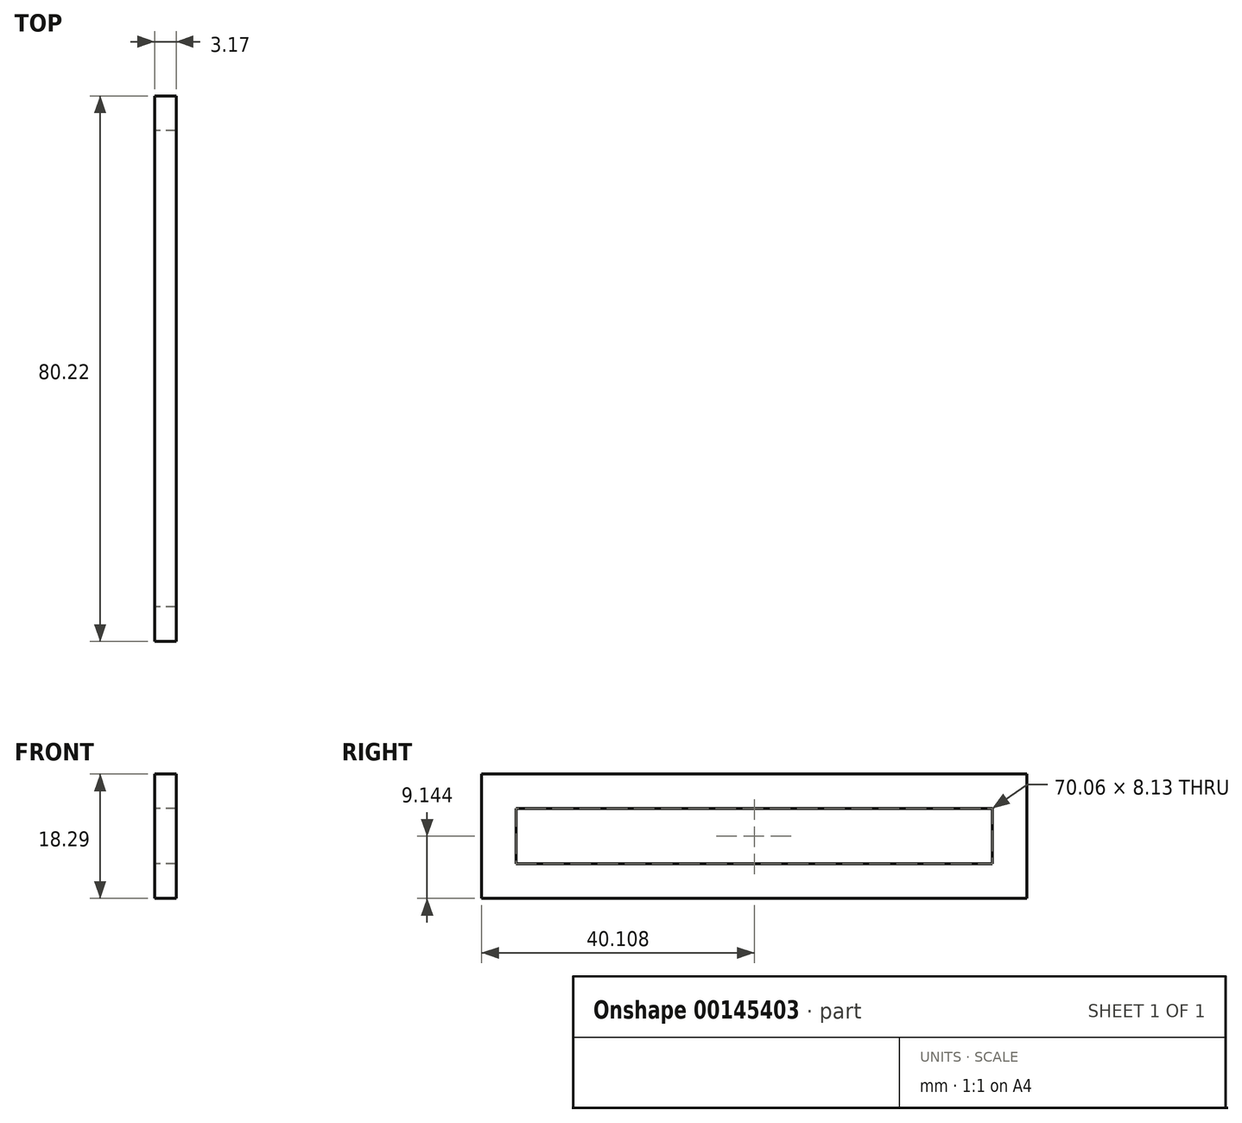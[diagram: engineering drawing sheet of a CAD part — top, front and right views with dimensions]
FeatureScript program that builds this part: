
annotation { "Feature Type Name" : "Feature", "Feature Type Description" : "" }
export const myFeature = defineFeature(function(context is Context, id is Id, definition is map)
    precondition{}
    {
        {
            var Q0;
            Q0=qCreatedBy(makeId("Right.planeOp"),FACE);
            var sketch = newSketch(context, id + "F0", { "sketchPlane" : qUnion([Q0])});
            skLineSegment(sketch, "E0.bottom", {"start": v(-40.28, 0) * mm, "end": v(-1.59, 0) * mm});
            skLineSegment(sketch, "E0.top", {"start": v(-40.28, 18.29) * mm, "end": v(-1.59, 18.29) * mm});
            skLineSegment(sketch, "E0.left", {"start": v(-40.28, 0) * mm, "end": v(-40.28, 18.29) * mm});
            skLineSegment(sketch, "E0.right", {"start": v(39.94, 0) * mm, "end": v(39.94, 18.29) * mm});
            skPoint(sketch, "E1.middle", {"position": v(0, 0) * mm});
            skPoint(sketch, "E1.bottom.start.orphan", {"position": v(-1.59, 22.3) * mm});
            skPoint(sketch, "E2.orphan", {"position": v(1.59, 22.3) * mm});
            skLineSegment(sketch, "E3.trimOffspring", {"start": v(1.59, 18.29) * mm, "end": v(39.94, 18.29) * mm});
            skPoint(sketch, "E4.orphan", {"position": v(-1.59, -22.3) * mm});
            skPoint(sketch, "E5.orphan", {"position": v(1.59, -22.3) * mm});
            skLineSegment(sketch, "E6.trimOffspring", {"start": v(1.59, 0) * mm, "end": v(39.94, 0) * mm});
            skLineSegment(sketch, "E7", {"start": v(-1.59, 18.29) * mm, "end": v(1.59, 18.29) * mm});
            skLineSegment(sketch, "E8", {"start": v(-1.59, 0) * mm, "end": v(1.59, 0) * mm});
            skLineSegment(sketch, "E9.0", {"start": v(-35.2, 5.08) * mm, "end": v(-1.59, 5.08) * mm});
            skLineSegment(sketch, "E9.1", {"start": v(-1.59, 5.08) * mm, "end": v(1.59, 5.08) * mm});
            skLineSegment(sketch, "E9.2", {"start": v(-35.2, 5.08) * mm, "end": v(-35.2, 13.2) * mm});
            skLineSegment(sketch, "E9.3", {"start": v(1.59, 5.08) * mm, "end": v(34.86, 5.08) * mm});
            skLineSegment(sketch, "E9.4", {"start": v(-35.2, 13.2) * mm, "end": v(-1.59, 13.2) * mm});
            skLineSegment(sketch, "E9.5", {"start": v(-1.59, 13.2) * mm, "end": v(1.59, 13.2) * mm});
            skLineSegment(sketch, "E9.6", {"start": v(1.59, 13.2) * mm, "end": v(34.86, 13.2) * mm});
            skLineSegment(sketch, "E9.7", {"start": v(34.86, 5.08) * mm, "end": v(34.86, 13.2) * mm});
            skSolve(sketch);
        }
        {
            var Q0;
            Q0=makeQuery(id+"F0.imprint","IMPRINT",FACE,{"disambiguationData":[TD([[makeQuery(id+"F0.imprint","IMPRINT",EDGE,{"derivedFrom":sQuery(id+"F0.wireOp",EDGE,"E0.bottom")}),1.0]])]});
            extrude(context, id + "F1", {"entities" : qUnion([Q0]), "depth" : 3.17 * mm});
        }
    });
